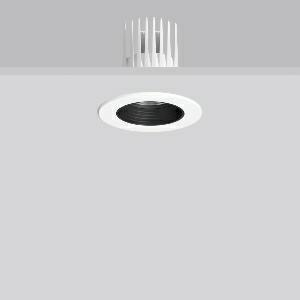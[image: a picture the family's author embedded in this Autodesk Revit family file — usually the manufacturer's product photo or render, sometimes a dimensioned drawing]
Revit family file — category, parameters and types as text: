
# Revit family: heledon_mini_e_901747_002_2_b7e8
name_source: partatom
category: Lighting Fixtures
units: mm (PartAtom-declared; Revit-internal decimal feet)

## family parameters
Cut with Voids When Loaded = No
Host = Face
Light Source = No
Part Type = Normal
Room Calculation Point = No
Round Connector Dimension = Use Diameter
Shared = No

## types (1)
- HELEDON mini E (1 x LED Modul 927, 1850 lm, 2700)
    Apparent Load = 20 VA
    Approval mark = CE
    CIE Flux Codes = 95 100 100 100 100
    Color Rendering = 92
    Color Temperature = 2700
    Default Elevation = 1800 mm
    Description = Series: HELEDON mini
Round recessed downlight. Housing: die-cast aluminium, powder-coated. Black plastic ring and recessed LED to prevent glare from the side. Optical assembly with lens made of plastic (polycarbonate) for the best homogeneous light distribution - can be changed without tools. Best colour rendering index Ra>90. Suitable for Recessed ceiling mounting. Installation without tools thanks to spring fastening system. Including separate LED converter with connecting cable 600 mm.High quality converter without flickering and stroboscopic effect. Through-wiring box (5 pole) available as accessory. The following accessories can be mounted without use of tools: interchangeable lenses, decorative glasses, honeycomb louvre, clear and frosted diffusers, white interchangeable plastic ring. 
Colour: traffic white, matt (RAL 9016)
Diameter: 124 mm
Height: 3 mm
Cut-out diameter: 114 mm
Recess height: 170 mm
Luminaire: recess height: 120 mm
Lamp: LED
Socket: without socket
Colour temperature: 2700K
Colour rendering index (CRI): 92
System power: 20 W
Rated luminous flux: 1850 lm
Luminous efficiency: 93 lm/W
Control gear: Regulated power supply
Protection class: II
Type of protection: IP 20
    Height = 0 mm  [stored 0 ft]
    Lamp = 1 x LED Modul 927
    Lamp Light Flux = 1850 lm
    Lamp count = 1
    Length = 124 mm  [stored 0.406824 ft]
    Lifetime = 50000 h
    Luminous efficacy = 93 lm/W
    Manufacturer = RZB
    ModVariant = No
    Model = 901747.002.2
    Mounting Place = Ceiling
    Mounting Type = Recessed
    Number of Poles = 1
    OnlyDefault = Yes
    Power Factor = 1
    Product Name = HELEDON mini E
    Product group = Recessed downlights
    ProductGroupID = 402
    Protection Class = Protection class II
    Protection Degree = IP 20
    RLX_Detail_Level = 1
    RLX_Emergency_Light_Flux = 0 lm
    RLX_Emergency_Type = 0
    RLX_Emergency_Type_DB = No
    RlxData = <blob elided: 131761 chars, md5=0785ce6b>
    Socket = socket
    Standby Power = 0 W
    System Light Flux = 1850 lm
    System Power = 20 W
    Type Comments = Product without accessories
    Type Image = 901656.002.jpg
    URL = http://relux.com
    VarID = ---
    Voltage = 230 V
    Voltage Range = 220-240 V
    Weight = 0.00 kg
    Width = 0 mm  [stored 0 ft]

note: [stored X ft] marks values corroborated as IEEE doubles in the binary element streams (Revit-internal decimal feet)

## geometry (parser evidence)
native form markers: Blend x4, Sweep x10
no freeform markers — native parametric forms only
